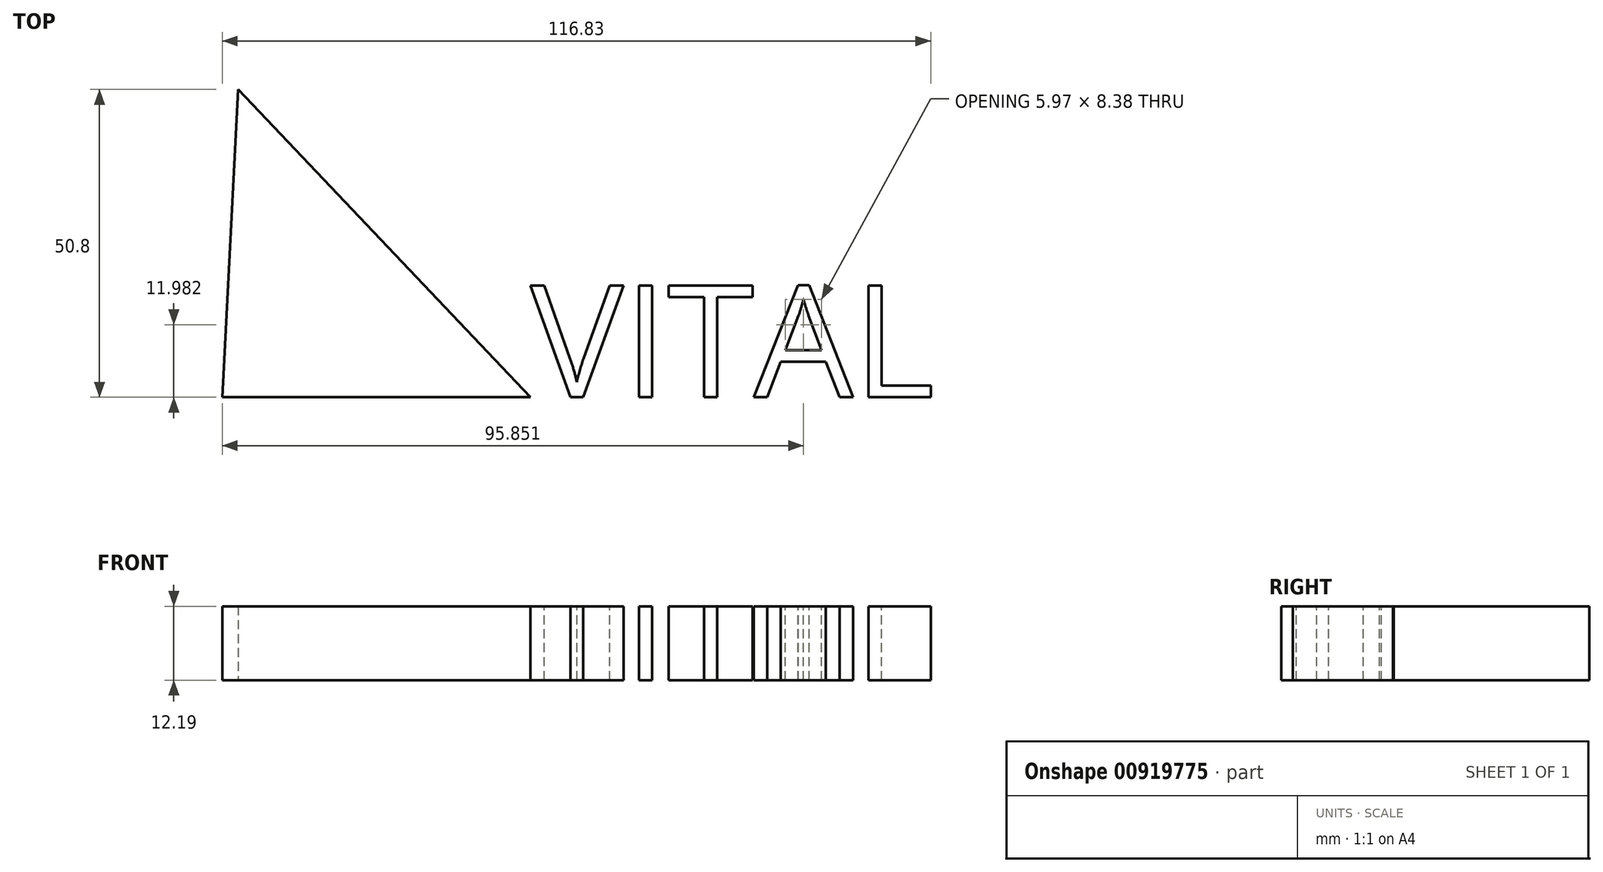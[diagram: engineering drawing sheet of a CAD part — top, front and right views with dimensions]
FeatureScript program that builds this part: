
annotation { "Feature Type Name" : "Feature", "Feature Type Description" : "" }
export const myFeature = defineFeature(function(context is Context, id is Id, definition is map)
    precondition{}
    {
        {
            var Q0;
            Q0=qCreatedBy(makeId("Top.planeOp"),FACE);
            var sketch = newSketch(context, id + "F0", { "sketchPlane" : qUnion([Q0])});
            skLineSegment(sketch, "E0.bottom", {"start": v(0, 0) * mm, "end": v(-50.8, 0) * mm});
            skLineSegment(sketch, "E0.right", {"start": v(-50.8, 0) * mm, "end": v(-48.16, 50.8) * mm});
            skLineSegment(sketch, "E1", {"start": v(0, 0) * mm, "end": v(-48.16, 50.8) * mm});
            skSolve(sketch);
        }
        {
            var Q0;
            Q0 = qSketchRegion(id + "F0", true);
            extrude(context, id + "F1", {"entities" : qUnion([Q0]), "depth" : 12.2 * mm, "offsetDistance" : 25.4 * mm});
        }
        {
            var Q0;
            Q0=makeQuery(id+"F1.opExtrude","CAP_FACE",FACE,{"disambiguationData":[OSD([sQuery(id+"F0.wireOp",EDGE,"E0.bottom"),sQuery(id+"F0.wireOp",EDGE,"E0.right"),sQuery(id+"F0.wireOp",EDGE,"E1")])],"isStart":false});
            var sketch = newSketch(context, id + "F2", { "sketchPlane" : qUnion([Q0])});
            skText(sketch, "E2", { "text": "VITAL", "fontName": "OpenSans-Regular.ttf"});
            const initialGuessF2  = {"E2": [0, 0, 1, 0, 0.0186]};
            skSetInitialGuess(sketch, initialGuessF2);
            skSolve(sketch);
        }
        {
            var Q0;
            Q0 = qSketchRegion(id + "F2", true);
            extrude(context, id + "F3", {"entities" : qUnion([Q0]), "oppositeDirection" : true, "depth" : 12.2 * mm, "offsetDistance" : 25.4 * mm});
        }
    });
